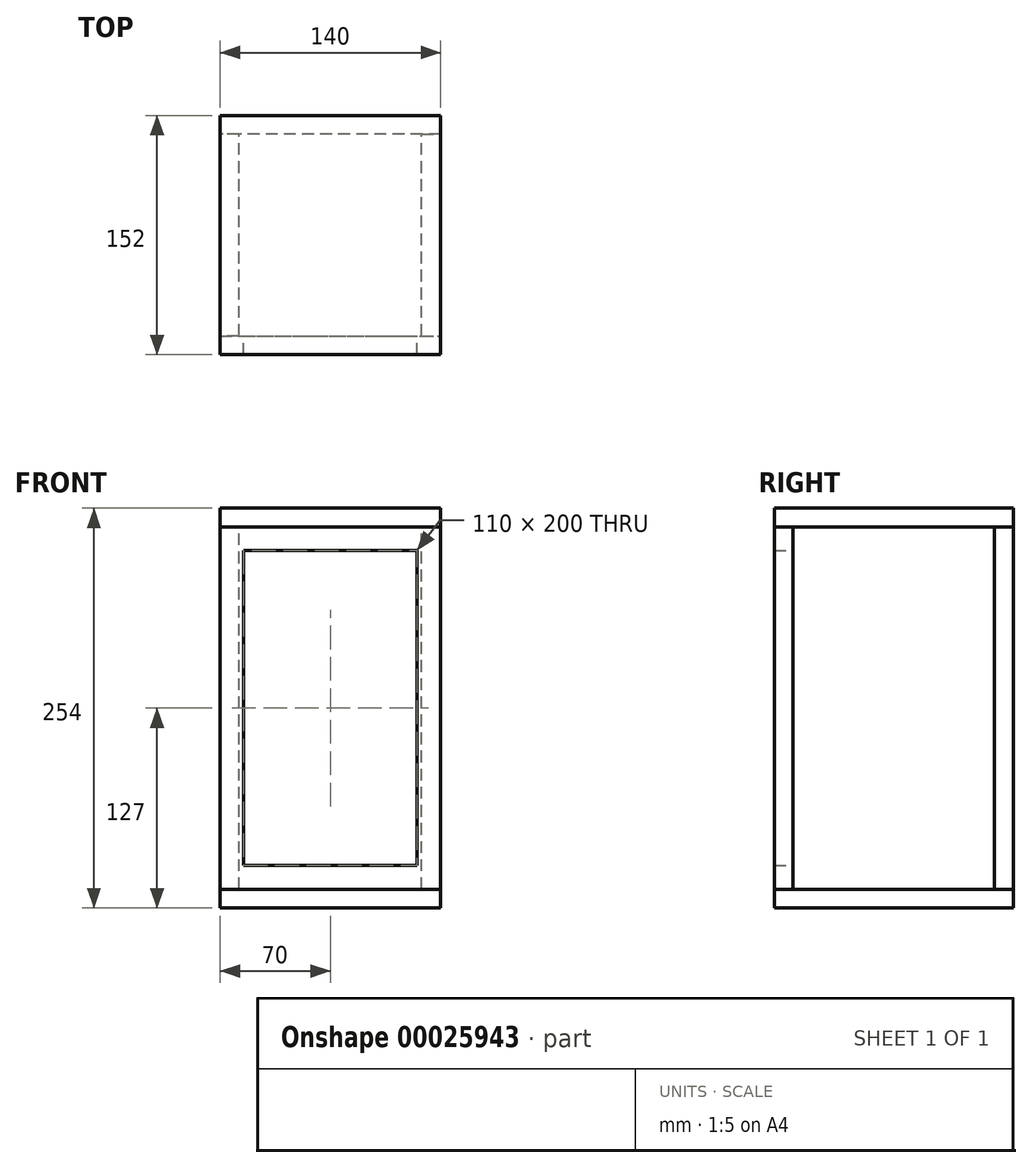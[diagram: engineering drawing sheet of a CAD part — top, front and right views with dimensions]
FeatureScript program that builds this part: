
annotation { "Feature Type Name" : "Feature", "Feature Type Description" : "" }
export const myFeature = defineFeature(function(context is Context, id is Id, definition is map)
    precondition{}
    {
        {
            var Q0;
            Q0=qCreatedBy(makeId("Front.planeOp"),FACE);
            var sketch = newSketch(context, id + "F0", { "sketchPlane" : qUnion([Q0])});
            skLineSegment(sketch, "E0.bottom", {"start": v(0, 0) * mm, "end": v(140, 0) * mm});
            skLineSegment(sketch, "E0.top", {"start": v(0, 230) * mm, "end": v(140, 230) * mm});
            skLineSegment(sketch, "E0.left", {"start": v(0, 0) * mm, "end": v(0, 230) * mm});
            skLineSegment(sketch, "E0.right", {"start": v(140, 0) * mm, "end": v(140, 230) * mm});
            skLineSegment(sketch, "E1.bottom", {"start": v(15, 215) * mm, "end": v(125, 215) * mm});
            skLineSegment(sketch, "E1.top", {"start": v(15, 15) * mm, "end": v(125, 15) * mm});
            skLineSegment(sketch, "E1.left", {"start": v(15, 215) * mm, "end": v(15, 15) * mm});
            skLineSegment(sketch, "E1.right", {"start": v(125, 215) * mm, "end": v(125, 15) * mm});
            skSolve(sketch);
        }
        {
            var Q0;
            Q0=makeQuery(id+"F0.imprint","IMPRINT",FACE,{"disambiguationData":[TD([[makeQuery(id+"F0.imprint","IMPRINT",EDGE,{"derivedFrom":sQuery(id+"F0.wireOp",EDGE,"E0.bottom")}),1.0]])]});
            extrude(context, id + "F1", {"entities" : qUnion([Q0]), "depth" : 12 * mm});
        }
        {
            var Q0;
            Q0=makeQuery(id+"F1.opExtrude","SWEPT_FACE",FACE,{"disambiguationData":[OSD([sQuery(id+"F0.wireOp",EDGE,"E0.top")])]});
            var sketch = newSketch(context, id + "F2", { "sketchPlane" : qUnion([Q0])});
            skLineSegment(sketch, "E2.bottom", {"start": v(0, -12) * mm, "end": v(140, -12) * mm});
            skLineSegment(sketch, "E2.top", {"start": v(0, 140) * mm, "end": v(140, 140) * mm});
            skLineSegment(sketch, "E2.left", {"start": v(0, -12) * mm, "end": v(0, 140) * mm});
            skLineSegment(sketch, "E2.right", {"start": v(140, -12) * mm, "end": v(140, 140) * mm});
            skSolve(sketch);
        }
        {
            var Q0;
            {var subQ1=sQuery(id+"F2.wireOp",EDGE,"E2.top");Q0=makeQuery(id+"F2.imprint","IMPRINT",FACE,{"disambiguationData":[TD([[makeQuery(id+"F2.imprint","IMPRINT",EDGE,{"derivedFrom":subQ1}),-1.0]])]});}
            var Q1;
            {var subQ2=sQuery(id+"F2.wireOp",EDGE,"E2.bottom");Q1=makeQuery(id+"F2.imprint","IMPRINT",FACE,{"disambiguationData":[TD([[makeQuery(id+"F2.imprint","IMPRINT",EDGE,{"derivedFrom":subQ2}),1.0]])]});}
            extrude(context, id + "F3", {"entities" : qUnion([Q0, Q1]), "depth" : 12 * mm});
        }
        {
            var Q0;
            Q0=makeQuery(id+"F1.opExtrude","SWEPT_FACE",FACE,{"disambiguationData":[OSD([sQuery(id+"F0.wireOp",EDGE,"E0.right")])]});
            var sketch = newSketch(context, id + "F4", { "sketchPlane" : qUnion([Q0])});
            skLineSegment(sketch, "E3.bottom", {"start": v(0, 0) * mm, "end": v(128, 0) * mm});
            skLineSegment(sketch, "E3.top", {"start": v(0, 230) * mm, "end": v(128, 230) * mm});
            skLineSegment(sketch, "E3.left", {"start": v(0, 0) * mm, "end": v(0, 230) * mm});
            skLineSegment(sketch, "E3.right", {"start": v(128, 0) * mm, "end": v(128, 230) * mm});
            skSolve(sketch);
        }
        {
            var Q0;
            Q0=makeQuery(id+"F4.imprint","IMPRINT",FACE,{"disambiguationData":[TD([[makeQuery(id+"F4.imprint","IMPRINT",EDGE,{"derivedFrom":sQuery(id+"F4.wireOp",EDGE,"E3.bottom")}),1.0]])]});
            extrude(context, id + "F5", {"entities" : qUnion([Q0]), "oppositeDirection" : true, "depth" : 12 * mm});
        }
        {
            var Q0;
            Q0=makeQuery(id+"F5.opExtrude","SWEPT_FACE",FACE,{"disambiguationData":[OSD([sQuery(id+"F4.wireOp",EDGE,"E3.right")])]});
            var sketch = newSketch(context, id + "F6", { "sketchPlane" : qUnion([Q0])});
            skLineSegment(sketch, "E4.bottom", {"start": v(-140, 230) * mm, "end": v(0, 230) * mm});
            skLineSegment(sketch, "E4.top", {"start": v(-140, 0) * mm, "end": v(0, 0) * mm});
            skLineSegment(sketch, "E4.left", {"start": v(-140, 230) * mm, "end": v(-140, 0) * mm});
            skLineSegment(sketch, "E4.right", {"start": v(0, 230) * mm, "end": v(0, 0) * mm});
            skSolve(sketch);
        }
        {
            var Q0;
            {var subQ1=sQuery(id+"F6.wireOp",EDGE,"E4.right");Q0=makeQuery(id+"F6.imprint","IMPRINT",FACE,{"disambiguationData":[TD([[makeQuery(id+"F6.imprint","IMPRINT",EDGE,{"derivedFrom":subQ1}),-1.0]])]});}
            var Q1;
            {var subQ1=sQuery(id+"F6.wireOp",EDGE,"E4.left");Q1=makeQuery(id+"F6.imprint","IMPRINT",FACE,{"disambiguationData":[TD([[makeQuery(id+"F6.imprint","IMPRINT",EDGE,{"derivedFrom":subQ1}),-1.0]])]});}
            extrude(context, id + "F7", {"entities" : qUnion([Q0, Q1]), "depth" : 12 * mm});
        }
        {
            var Q0;
            Q0=makeQuery(id+"F1.opExtrude","SWEPT_FACE",FACE,{"disambiguationData":[OSD([sQuery(id+"F0.wireOp",EDGE,"E0.left")])]});
            var Q1;
            Q1=makeQuery(id+"F1.opExtrude","SWEPT_FACE",FACE,{"disambiguationData":[OSD([sQuery(id+"F0.wireOp",EDGE,"E0.right")])]});
            cPlane(context, id + "F8", {"entities" : qUnion([Q0, Q1]), "cplaneType" : CPlaneType.MID_PLANE, "offset" : 150 * mm, "width" : 150 * mm, "height" : 150 * mm});
        }
        {
            var Q0;
            Q0=makeQuery(id+"F5.opExtrude","SWEPT_BODY",BODY,{"disambiguationData":[OSD([sQuery(id+"F4.wireOp",EDGE,"E3.bottom"),sQuery(id+"F4.wireOp",EDGE,"E3.top"),sQuery(id+"F4.wireOp",EDGE,"E3.left"),sQuery(id+"F4.wireOp",EDGE,"E3.right")])]});
            var Q1;
            Q1=qCreatedBy(id+"F8.planeOp",FACE);
            mirror(context, id + "F9", {"entities" : qUnion([Q0]), "mirrorPlane" : qUnion([Q1])});
        }
        {
            var Q0;
            {var subQ2=sQuery(id+"F2.wireOp",EDGE,"E2.bottom");Q0=makeQuery(id+"F2.imprint","IMPRINT",FACE,{"disambiguationData":[TD([[makeQuery(id+"F2.imprint","IMPRINT",EDGE,{"derivedFrom":subQ2}),1.0]])]});}
            var Q1;
            Q1=makeQuery(id+"F1.opExtrude","SWEPT_FACE",FACE,{"disambiguationData":[OSD([sQuery(id+"F0.wireOp",EDGE,"E0.bottom")])]});
            cPlane(context, id + "F10", {"entities" : qUnion([Q0, Q1]), "cplaneType" : CPlaneType.MID_PLANE, "offset" : 150 * mm, "width" : 150 * mm, "height" : 150 * mm});
        }
        {
            var Q0;
            Q0=makeQuery(id+"F3.opExtrude","SWEPT_BODY",BODY,{"disambiguationData":[OSD([sQuery(id+"F2.wireOp",EDGE,"E2.bottom"),sQuery(id+"F2.wireOp",EDGE,"E2.top"),sQuery(id+"F2.wireOp",EDGE,"E2.left"),sQuery(id+"F2.wireOp",EDGE,"E2.right")])]});
            var Q1;
            Q1=qCreatedBy(id+"F10.planeOp",FACE);
            mirror(context, id + "F11", {"entities" : qUnion([Q0]), "mirrorPlane" : qUnion([Q1])});
        }
    });
